# Revit family: RN 18010 Filtro fine
name_source: partatom
category: Rohrzubehör
units: mm (PartAtom-declared; Revit-internal decimal feet)

## family parameters
Arbeitsebenenbasiert = Nein
Beim Laden mit Abzugskörper schneiden = Nein
Bemaßung runder Anschluss = Durchmesser verwenden
Gemeinsam genutzt = Nein
Immer vertikal = Ja
Teiletyp = Ventil - Zerlegung in

## types (4) — shared parameters
1.010.00.2 Blattnummer der Richtlinie = 17
1.010.00.3 Ausgabedatum (Monat) der Richtlinie = 201601
1.010.00.4 Herstellername = R. Nussbaum AG
1.010.00.5 Revisionsdatum der Datei = 20190528
1.010.00.6 Webadresse des Herstellers = http://www.nussbaum.ch
1.100.00.3 Sortiernummer für Anzeigereihenfolge = 9
1.100.00.4 Produktbezeichnung = Filterkombination, Filter und Schmutzfänger
1.960/3L.00.8 Link (URL) = https://www.nussbaum.ch
17.700.00.4 Armaturentyp = 1
17.700.00.7 Maximale Betriebstemperatur TB [°C] = 30
17.700.00.8 Maximaler Betriebsdruck (Arbeitsdruck) ps [1.0 · 105 Pa] = 16
Connector Visibility = Nein
EnclosingSpace Visibility = Nein
Hersteller = R. Nussbauzm AG
URL = https://www.nussbaum.ch

## per-type parameters (varying)
| type | 1.800.00.3 TGA-Nummer | 1.810.00.3 Hersteller-Bestellnummer | 1.810.00.4 DATANORM-Nummer | 1.810.00.5 StLB-Nummer | 1.810.00.6 GTIN-Nummer | 17.700.00.30 Produktbeschreibung | 17.700.00.5 Nennweite DN | 17.700.00.6 kvs-Wert [m3/h] | CONNECTOR0_DIAMETER_dX_0r | CONNECTOR0_dX_00 | CONNECTOR0_dX_01 | CONNECTOR0_ref_dX | CONNECTOR1_DIAMETER_dX_0r | CONNECTOR1_dX_00 | CONNECTOR1_dX_01 | CONNECTOR1_ref_dX | Modell | R. Nussbaum AG 18010.06 de Visibility | R. Nussbaum AG 18010.07 de Visibility | R. Nussbaum AG 18010.08 de Visibility | R. Nussbaum AG 18010.09 de Visibility | Typenkommentare |
| DN 25 | 0090070000000000000000000000020070000000000000000100000000 | 18010.06 | 18010.06 | 617.125 | 7612945003263 | 18010.06, Feinfilter, DN=25, Rp=1 | 25 | 15.83 | 25 mm  [stored 0.082021 ft] | 85 mm | 68 mm | 68 mm | 25 mm  [stored 0.082021 ft] | 68 mm | 85 mm | 68 mm | 18010.06 | Ja | Nein | Nein | Nein | Filtro fineDN 25 |
| DN 32 | 0090070000000000000000000000020070000000000000000200000000 | 18010.07 | 18010.07 | 617.126 | 7612945003270 | 18010.07, Feinfilter, DN=32, Rp=1¼ | 32 | 18.11 | 30 mm | 92 mm | 73 mm | 73 mm | 30 mm | 73 mm | 92 mm | 73 mm | 18010.07 | Nein | Ja | Nein | Nein | Filtro fineDN 32 |
| DN 40 | 0090070000000000000000000000020070000000000000000300000000 | 18010.08 | 18010.08 | 617.127 | 7612945003287 | 18010.08, Feinfilter, DN=40, Rp=1½ | 40 | 18.11 | 40 mm | 97 mm | 78 mm  [stored 0.255906 ft] | 78 mm  [stored 0.255906 ft] | 40 mm | 78 mm  [stored 0.255906 ft] | 97 mm | 78 mm  [stored 0.255906 ft] | 18010.08 | Nein | Nein | Ja | Nein | Filtro fineDN 40 |
| DN 50 | 0090070000000000000000000000020070000000000000000400000000 | 18010.09 | 18010.09 | 617.128 | 7612945003294 | 18010.09, Feinfilter, DN=50, Rp=2 | 50 | 19.59 | 50 mm | 103 mm | 79 mm | 79 mm | 50 mm | 79 mm | 103 mm | 79 mm | 18010.09 | Nein | Nein | Nein | Ja | Filtro fineDN 50 |

note: [stored X ft] marks values corroborated as IEEE doubles in the binary element streams (Revit-internal decimal feet)

## geometry (parser evidence)
native form markers: Sweep x1
no freeform markers — native parametric forms only
